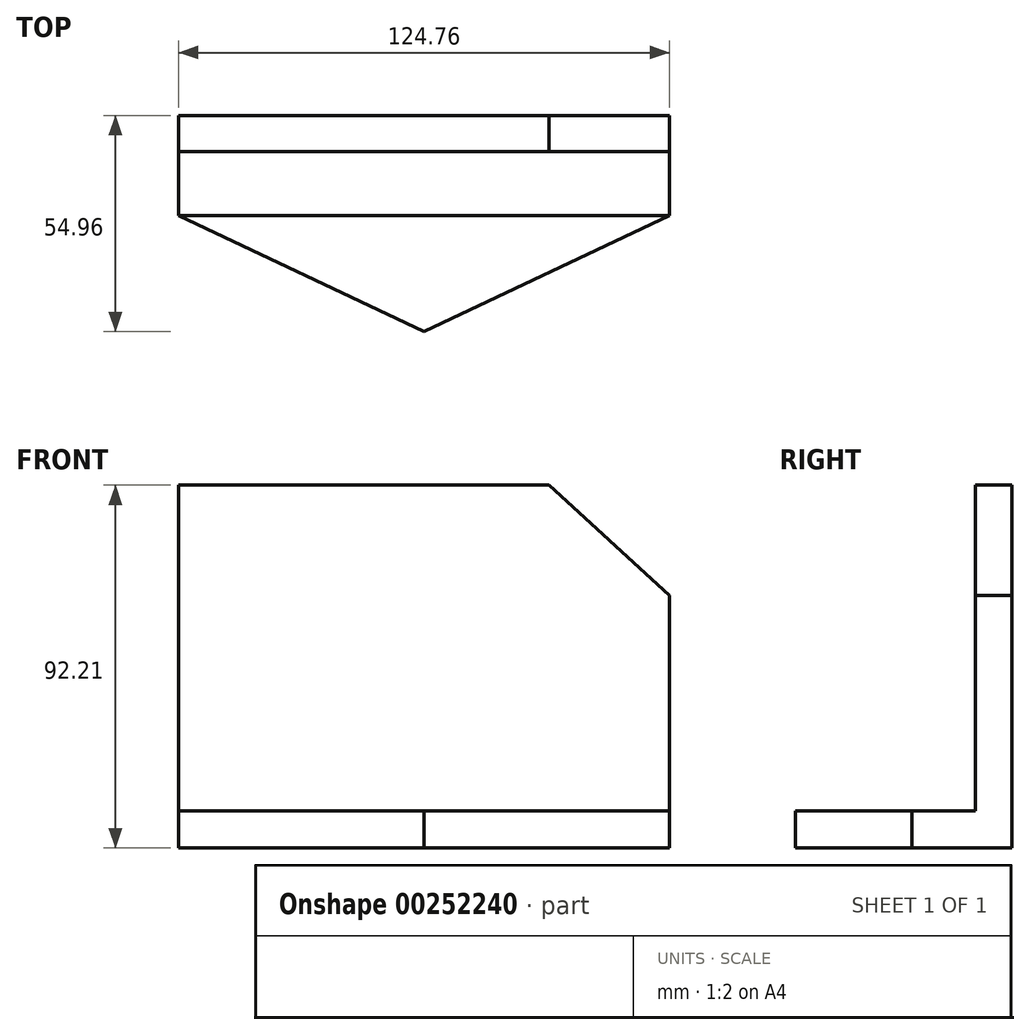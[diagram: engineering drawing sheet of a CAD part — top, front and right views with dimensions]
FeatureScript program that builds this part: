
annotation { "Feature Type Name" : "Feature", "Feature Type Description" : "" }
export const myFeature = defineFeature(function(context is Context, id is Id, definition is map)
    precondition{}
    {
        {
            var Q0;
            Q0=qCreatedBy(makeId("Front.planeOp"),FACE);
            var sketch = newSketch(context, id + "F0", { "sketchPlane" : qUnion([Q0])});
            skLineSegment(sketch, "E0.bottom", {"start": v(-62.38, 45.62) * mm, "end": v(62.38, 45.62) * mm});
            skLineSegment(sketch, "E0.top", {"start": v(-62.38, -46.5) * mm, "end": v(62.38, -46.5) * mm});
            skLineSegment(sketch, "E0.left", {"start": v(-62.38, 45.62) * mm, "end": v(-62.38, -46.5) * mm});
            skLineSegment(sketch, "E0.right", {"start": v(62.38, 45.62) * mm, "end": v(62.38, -46.5) * mm});
            skSolve(sketch);
        }
        {
            var Q0;
            Q0 = qSketchRegion(id + "F0", true);
            extrude(context, id + "F1", {"entities" : qUnion([Q0]), "depth" : 25.4 * mm});
        }
        {
            var Q0;
            Q0=makeQuery(id+"F1.opExtrude","SWEPT_FACE",FACE,{"disambiguationData":[OSD([sQuery(id+"F0.wireOp",EDGE,"E0.bottom")])]});
            var sketch = newSketch(context, id + "F2", { "sketchPlane" : qUnion([Q0])});
            skLineSegment(sketch, "E1", {"start": v(-62.38, -9.18) * mm, "end": v(62.38, -9.18) * mm});
            skSolve(sketch);
        }
        {
            var Q0;
            {var subQ0=sQuery(id+"F2.wireOp",EDGE,"E1");Q0=makeQuery(id+"F2.imprint","IMPRINT",FACE,{"disambiguationData":[TD([[makeQuery(id+"F2.imprint","IMPRINT",EDGE,{"derivedFrom":subQ0}),-1.0]])]});}
            extrude(context, id + "F3", {"entities" : qUnion([Q0]), "operationType" : NewBodyOperationType.REMOVE, "oppositeDirection" : true, "depth" : 82.8 * mm});
        }
        {
            var Q0;
            Q0=makeQuery(id+"F3.boolean.opBoolean","COPY",FACE,{"derivedFrom":makeQuery(id+"F3.opExtrude","SWEPT_FACE",FACE,{"disambiguationData":[OSD([sQuery(id+"F2.wireOp",EDGE,"E1")])]})});
            var sketch = newSketch(context, id + "F4", { "sketchPlane" : qUnion([Q0])});
            skLineSegment(sketch, "E2", {"start": v(-31.77, 45.62) * mm, "end": v(-62.38, 17.63) * mm});
            skLineSegment(sketch, "E3", {"start": v(-62.38, 17.63) * mm, "end": v(-31.77, 45.62) * mm});
            skLineSegment(sketch, "E4", {"start": v(31.77, 45.62) * mm, "end": v(62.38, 17.63) * mm});
            skSolve(sketch);
        }
        {
            var Q0;
            {var subQ0=sQuery(id+"F4.wireOp",EDGE,"E4");Q0=makeQuery(id+"F4.imprint","IMPRINT",FACE,{"disambiguationData":[TD([[makeQuery(id+"F4.imprint","IMPRINT",EDGE,{"derivedFrom":subQ0}),1.0]])]});}
            var Q1;
            {var subQ0=sQuery(id+"F4.wireOp",EDGE,"E3");Q1=makeQuery(id+"F4.imprint","IMPRINT",FACE,{"disambiguationData":[TD([[makeQuery(id+"F4.imprint","IMPRINT",EDGE,{"derivedFrom":subQ0}),1.0]])]});}
            extrude(context, id + "F5", {"entities" : qUnion([Q0, Q1]), "operationType" : NewBodyOperationType.REMOVE, "oppositeDirection" : true, "depth" : 25.4 * mm});
        }
        {
            var Q0;
            Q0=makeQuery(id+"F3.boolean.opBoolean","COPY",FACE,{"derivedFrom":makeQuery(id+"F3.opExtrude","CAP_FACE",FACE,{"disambiguationData":[OSD([sQuery(id+"F0.wireOp",EDGE,"E0.bottom"),sQuery(id+"F0.wireOp",EDGE,"E0.left"),sQuery(id+"F0.wireOp",EDGE,"E0.right"),sQuery(id+"F2.wireOp",EDGE,"E1")])],"isStart":false})});
            var sketch = newSketch(context, id + "F6", { "sketchPlane" : qUnion([Q0])});
            skLineSegment(sketch, "E5", {"start": v(-62.38, -25.4) * mm, "end": v(0, -54.96) * mm});
            skLineSegment(sketch, "E6", {"start": v(0, -54.96) * mm, "end": v(62.38, -25.4) * mm});
            skSolve(sketch);
        }
        {
            var Q0;
            Q0=makeQuery(id+"F6.imprint","IMPRINT",FACE,{"disambiguationData":[TD([[makeQuery(id+"F6.imprint","IMPRINT",EDGE,{"derivedFrom":sQuery(id+"F6.wireOp",EDGE,"E5")}),1.0]])]});
            extrude(context, id + "F7", {"entities" : qUnion([Q0]), "oppositeDirection" : true, "depth" : 9.4 * mm});
        }
    });
